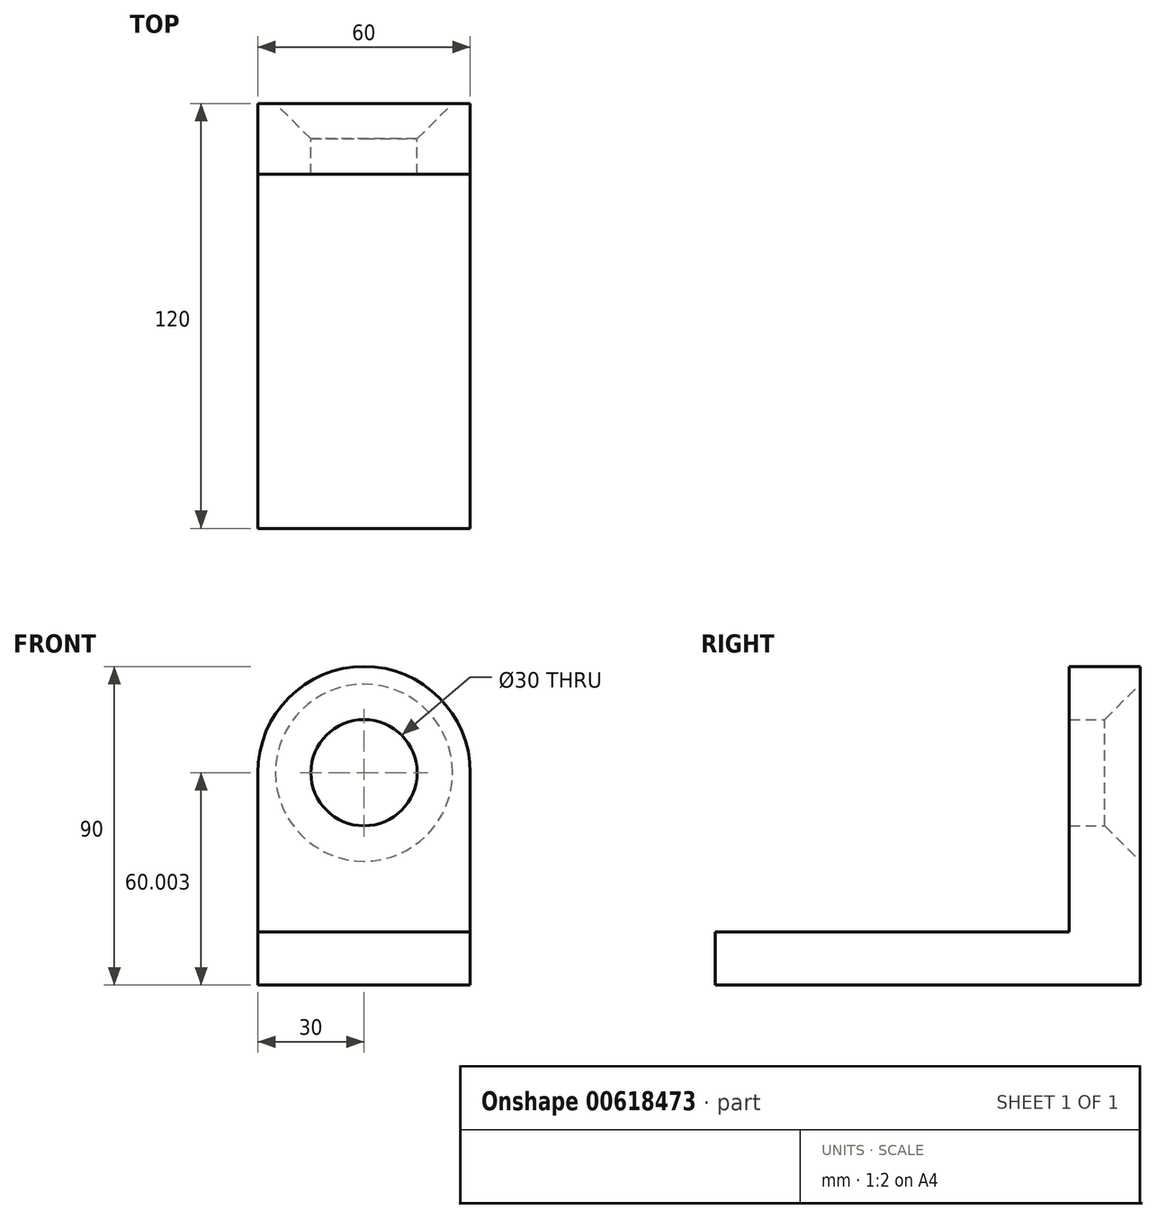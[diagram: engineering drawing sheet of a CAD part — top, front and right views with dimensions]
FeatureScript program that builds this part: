
annotation { "Feature Type Name" : "Feature", "Feature Type Description" : "" }
export const myFeature = defineFeature(function(context is Context, id is Id, definition is map)
    precondition{}
    {
        {
            var Q0;
            Q0=qCreatedBy(makeId("Front.planeOp"),FACE);
            var sketch = newSketch(context, id + "F0", { "sketchPlane" : qUnion([Q0])});
            skLineSegment(sketch, "E0.top", {"start": v(30, -49.72) * mm, "end": v(-30, -49.72) * mm});
            skLineSegment(sketch, "E0.left", {"start": v(30, 10.28) * mm, "end": v(30, -49.72) * mm});
            skLineSegment(sketch, "E0.right", {"start": v(-30, 10.28) * mm, "end": v(-30, -49.72) * mm});
            skPoint(sketch, "E0.middle", {"position": v(0, 0) * mm});
            skCircle(sketch, "E1", {"center": v(0, 10.28) * mm, "radius": 15 * mm});
            skArc(sketch, "E2", {"start": v(30, 10.28) * mm, "mid": v(0, 40.28) * mm, "end": v(-30, 10.28) * mm});
            skPoint(sketch, "E3.orphan", {"position": v(30, 49.72) * mm});
            skPoint(sketch, "E4.orphan", {"position": v(-30, 49.72) * mm});
            skSolve(sketch);
        }
        {
            var Q0;
            Q0=makeQuery(id+"F0.imprint","IMPRINT",FACE,{"disambiguationData":[TD([[makeQuery(id+"F0.imprint","IMPRINT",EDGE,{"derivedFrom":sQuery(id+"F0.wireOp",EDGE,"E0.top")}),-1.0]])]});
            extrude(context, id + "F1", {"entities" : qUnion([Q0]), "depth" : 20 * mm, "offsetDistance" : 25 * mm});
        }
        {
            var Q0;
            Q0=makeQuery(id+"F1.opExtrude","CAP_FACE",FACE,{"disambiguationData":[OSD([sQuery(id+"F0.wireOp",EDGE,"E0.top"),sQuery(id+"F0.wireOp",EDGE,"E0.left"),sQuery(id+"F0.wireOp",EDGE,"E0.right"),sQuery(id+"F0.wireOp",EDGE,"E1"),sQuery(id+"F0.wireOp",EDGE,"E2")])],"isStart":false});
            var sketch = newSketch(context, id + "F2", { "sketchPlane" : qUnion([Q0])});
            skLineSegment(sketch, "E5.bottom", {"start": v(-30, -49.72) * mm, "end": v(30, -49.72) * mm});
            skLineSegment(sketch, "E5.top", {"start": v(-30, -34.72) * mm, "end": v(30, -34.72) * mm});
            skLineSegment(sketch, "E5.left", {"start": v(-30, -49.72) * mm, "end": v(-30, -34.72) * mm});
            skLineSegment(sketch, "E5.right", {"start": v(30, -49.72) * mm, "end": v(30, -34.72) * mm});
            skSolve(sketch);
        }
        {
            var Q0;
            Q0=makeQuery(id+"F2.imprint","IMPRINT",FACE,{"disambiguationData":[TD([[makeQuery(id+"F2.imprint","IMPRINT",EDGE,{"derivedFrom":sQuery(id+"F2.wireOp",EDGE,"E5.bottom")}),-1.0]])]});
            extrude(context, id + "F3", {"entities" : qUnion([Q0]), "operationType" : NewBodyOperationType.ADD, "depth" : 100 * mm, "offsetDistance" : 25 * mm});
        }
        {
            var Q0;
            Q0=makeQuery(id+"F1.opExtrude","CAP_EDGE",EDGE,{"disambiguationData":[OSD([sQuery(id+"F0.wireOp",EDGE,"E1")])],"isStart":true});
            chamfer(context, id + "F4", {"entities" : qUnion([Q0]), "width" : 10 * mm, "tangentPropagation" : true});
        }
    });
